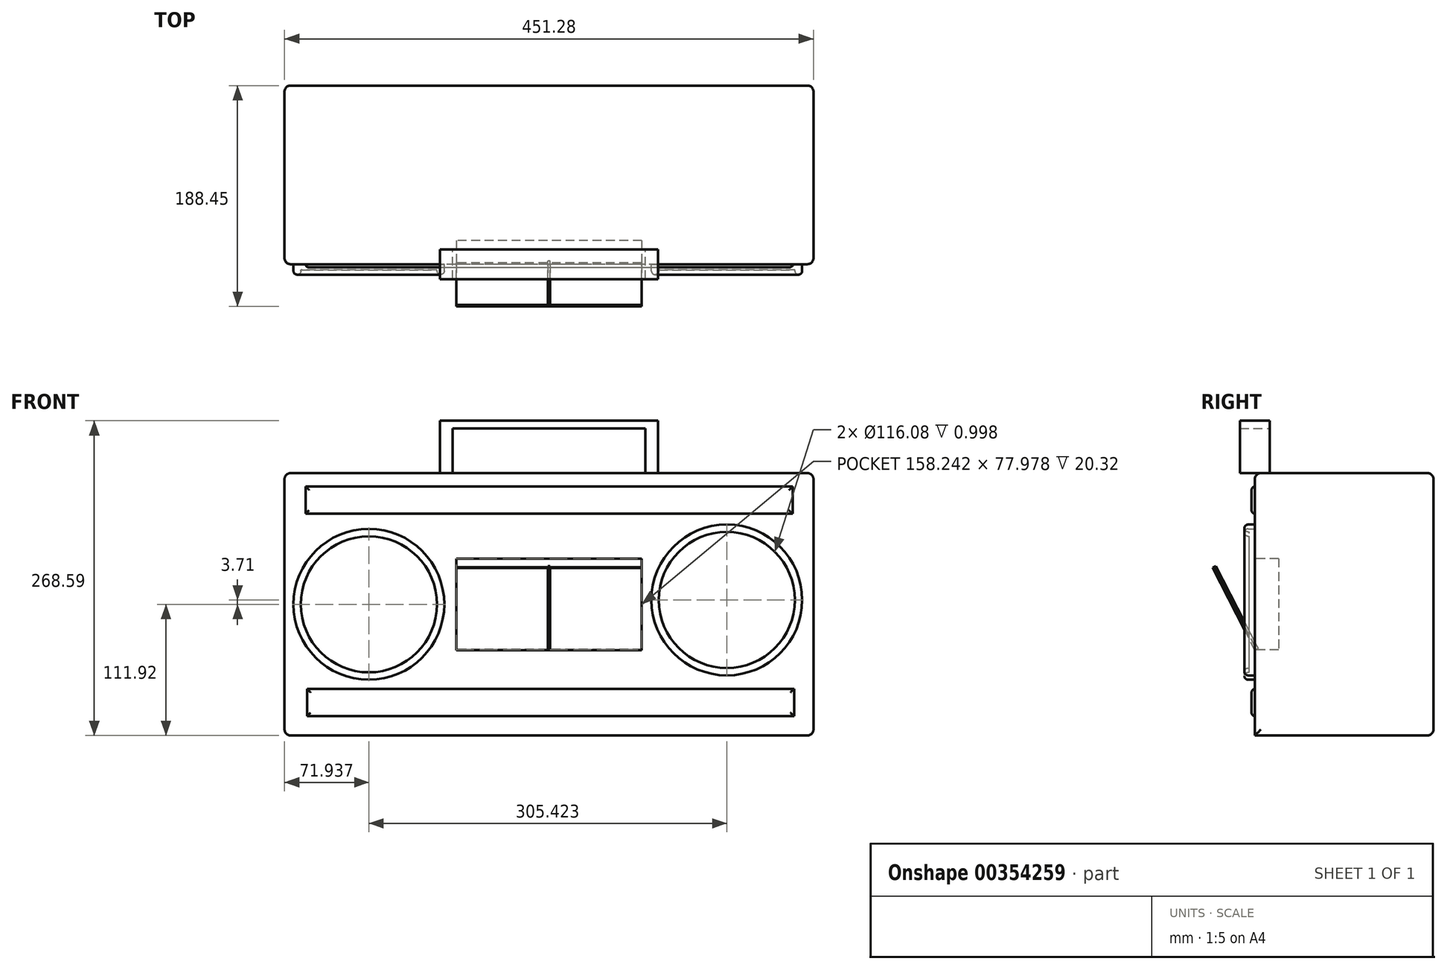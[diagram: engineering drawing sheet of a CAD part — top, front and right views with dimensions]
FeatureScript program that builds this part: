
annotation { "Feature Type Name" : "Feature", "Feature Type Description" : "" }
export const myFeature = defineFeature(function(context is Context, id is Id, definition is map)
    precondition{}
    {
        {
            var Q0;
            Q0=qCreatedBy(makeId("Front.planeOp"),FACE);
            var sketch = newSketch(context, id + "F0", { "sketchPlane" : qUnion([Q0])});
            skLineSegment(sketch, "E0.bottom", {"start": v(79.12, 38.99) * mm, "end": v(-79.12, 38.99) * mm});
            skLineSegment(sketch, "E0.top", {"start": v(79.12, -38.99) * mm, "end": v(-79.12, -38.99) * mm});
            skLineSegment(sketch, "E0.left", {"start": v(79.12, 38.99) * mm, "end": v(79.12, -38.99) * mm});
            skLineSegment(sketch, "E0.right", {"start": v(-79.12, 38.99) * mm, "end": v(-79.12, -38.99) * mm});
            skPoint(sketch, "E0.middle", {"position": v(0, 0) * mm});
            skSolve(sketch);
        }
        {
            var Q0;
            Q0=qCreatedBy(makeId("Front.planeOp"),FACE);
            var sketch = newSketch(context, id + "F1", { "sketchPlane" : qUnion([Q0])});
            skLineSegment(sketch, "E1.bottom", {"start": v(225.64, 111.92) * mm, "end": v(-225.64, 111.92) * mm});
            skLineSegment(sketch, "E1.top", {"start": v(225.64, -111.92) * mm, "end": v(-225.64, -111.92) * mm});
            skLineSegment(sketch, "E1.left", {"start": v(225.64, 111.92) * mm, "end": v(225.64, -111.92) * mm});
            skLineSegment(sketch, "E1.right", {"start": v(-225.64, 111.92) * mm, "end": v(-225.64, -111.92) * mm});
            skPoint(sketch, "E1.middle", {"position": v(0, 0) * mm});
            skSolve(sketch);
        }
        {
            var Q0;
            Q0=makeQuery(id+"F1.imprint","IMPRINT",FACE,{"disambiguationData":[TD([[makeQuery(id+"F1.imprint","IMPRINT",EDGE,{"derivedFrom":sQuery(id+"F1.wireOp",EDGE,"E1.bottom")}),1.0]])]});
            extrude(context, id + "F2", {"entities" : qUnion([Q0]), "oppositeDirection" : true, "depth" : 152.4 * mm});
        }
        {
            var Q0;
            Q0=makeQuery(id+"F0.imprint","IMPRINT",FACE,{"disambiguationData":[TD([[makeQuery(id+"F0.imprint","IMPRINT",EDGE,{"derivedFrom":sQuery(id+"F0.wireOp",EDGE,"E0.bottom")}),1.0]])]});
            extrude(context, id + "F3", {"entities" : qUnion([Q0]), "operationType" : NewBodyOperationType.REMOVE, "oppositeDirection" : true, "depth" : 20.32 * mm});
        }
        {
            var Q0;
            Q0=qCreatedBy(makeId("Front.planeOp"),FACE);
            var sketch = newSketch(context, id + "F4", { "sketchPlane" : qUnion([Q0])});
            skCircle(sketch, "E2", {"center": v(-153.7, 0) * mm, "radius": 64.33 * mm});
            skCircle(sketch, "E3", {"center": v(151.72, 3.7) * mm, "radius": 64.33 * mm});
            skCircle(sketch, "E4", {"center": v(-153.7, 0) * mm, "radius": 58.04 * mm});
            skCircle(sketch, "E5", {"center": v(151.72, 3.7) * mm, "radius": 58.04 * mm});
            skSolve(sketch);
        }
        {
            var Q0;
            Q0=makeQuery(id+"F4.imprint","IMPRINT",FACE,{"disambiguationData":[TD([[makeQuery(id+"F4.imprint","IMPRINT",EDGE,{"derivedFrom":sQuery(id+"F4.wireOp",EDGE,"E2")}),1.0]])]});
            var Q1;
            Q1=makeQuery(id+"F4.imprint","IMPRINT",FACE,{"disambiguationData":[TD([[makeQuery(id+"F4.imprint","IMPRINT",EDGE,{"derivedFrom":sQuery(id+"F4.wireOp",EDGE,"E3")}),1.0]])]});
            extrude(context, id + "F5", {"entities" : qUnion([Q0, Q1]), "operationType" : NewBodyOperationType.ADD, "depth" : 8.9 * mm});
        }
        {
            var Q0;
            Q0=makeQuery(id+"F4.imprint","IMPRINT",FACE,{"disambiguationData":[TD([[makeQuery(id+"F4.imprint","IMPRINT",EDGE,{"derivedFrom":sQuery(id+"F4.wireOp",EDGE,"E5")}),1.0]])]});
            var Q1;
            Q1=makeQuery(id+"F4.imprint","IMPRINT",FACE,{"disambiguationData":[TD([[makeQuery(id+"F4.imprint","IMPRINT",EDGE,{"derivedFrom":sQuery(id+"F4.wireOp",EDGE,"E4")}),1.0]])]});
            extrude(context, id + "F6", {"entities" : qUnion([Q0, Q1]), "operationType" : NewBodyOperationType.ADD, "depth" : 4.83 * mm});
        }
        {
            var Q0;
            Q0=qCreatedBy(makeId("Front.planeOp"),FACE);
            var sketch = newSketch(context, id + "F7", { "sketchPlane" : qUnion([Q0])});
            skLineSegment(sketch, "E6.bottom", {"start": v(207.8, 100.54) * mm, "end": v(-207.8, 100.54) * mm});
            skLineSegment(sketch, "E6.top", {"start": v(207.8, 77.23) * mm, "end": v(-207.8, 77.23) * mm});
            skLineSegment(sketch, "E6.left", {"start": v(207.8, 100.54) * mm, "end": v(207.8, 77.23) * mm});
            skLineSegment(sketch, "E6.right", {"start": v(-207.8, 100.54) * mm, "end": v(-207.8, 77.23) * mm});
            skPoint(sketch, "E6.middle", {"position": v(0, 88.89) * mm});
            skLineSegment(sketch, "E7.bottom", {"start": v(209.06, -72.15) * mm, "end": v(-206.54, -72.15) * mm});
            skLineSegment(sketch, "E7.top", {"start": v(209.06, -95.47) * mm, "end": v(-206.54, -95.47) * mm});
            skLineSegment(sketch, "E7.left", {"start": v(209.06, -72.15) * mm, "end": v(209.06, -95.47) * mm});
            skLineSegment(sketch, "E7.right", {"start": v(-206.54, -72.15) * mm, "end": v(-206.54, -95.47) * mm});
            skPoint(sketch, "E7.middle", {"position": v(1.26, -83.8) * mm});
            skSolve(sketch);
        }
        {
            var Q0;
            Q0=makeQuery(id+"F7.imprint","IMPRINT",FACE,{"disambiguationData":[TD([[makeQuery(id+"F7.imprint","IMPRINT",EDGE,{"derivedFrom":sQuery(id+"F7.wireOp",EDGE,"E6.bottom")}),1.0]])]});
            var Q1;
            Q1=makeQuery(id+"F7.imprint","IMPRINT",FACE,{"disambiguationData":[TD([[makeQuery(id+"F7.imprint","IMPRINT",EDGE,{"derivedFrom":sQuery(id+"F7.wireOp",EDGE,"E7.bottom")}),1.0]])]});
            extrude(context, id + "F8", {"entities" : qUnion([Q0, Q1]), "operationType" : NewBodyOperationType.ADD, "depth" : 2.8 * mm});
        }
        {
            var Q0;
            Q0=qCreatedBy(makeId("Right.planeOp"),FACE);
            var sketch = newSketch(context, id + "F9", { "sketchPlane" : qUnion([Q0])});
            skLineSegment(sketch, "E8", {"start": v(0, -39.04) * mm, "end": v(-36.05, 31.26) * mm});
            skLineSegment(sketch, "E9", {"start": v(-36.05, 31.26) * mm, "end": v(-33.34, 32.65) * mm});
            skLineSegment(sketch, "E10", {"start": v(0, -39.04) * mm, "end": v(2.72, -37.65) * mm});
            skLineSegment(sketch, "E11", {"start": v(-33.34, 32.65) * mm, "end": v(2.72, -37.65) * mm});
            skSolve(sketch);
        }
        {
            var Q0;
            Q0=makeQuery(id+"F9.imprint","IMPRINT",FACE,{"disambiguationData":[TD([[makeQuery(id+"F9.imprint","IMPRINT",EDGE,{"derivedFrom":sQuery(id+"F9.wireOp",EDGE,"E8")}),-1.0]])]});
            extrude(context, id + "F10", {"entities" : qUnion([Q0]), "endBound" : BoundingType.SYMMETRIC, "depth" : 1.78 * mm});
        }
        {
            var Q0;
            Q0=qCreatedBy(makeId("Right.planeOp"),FACE);
            var sketch = newSketch(context, id + "F11", { "sketchPlane" : qUnion([Q0])});
            skLineSegment(sketch, "E12", {"start": v(0, -39.04) * mm, "end": v(-35.9, 31.02) * mm});
            skLineSegment(sketch, "E13", {"start": v(-35.9, 31.02) * mm, "end": v(-34.7, 31.64) * mm});
            skLineSegment(sketch, "E14", {"start": v(-34.7, 31.64) * mm, "end": v(1.23, -38.47) * mm});
            skLineSegment(sketch, "E15", {"start": v(1.23, -38.47) * mm, "end": v(0, -39.04) * mm});
            skSolve(sketch);
        }
        {
            var Q0;
            Q0 = qSketchRegion(id + "F11", true);
            extrude(context, id + "F12", {"entities" : qUnion([Q0]), "endBound" : BoundingType.SYMMETRIC, "depth" : 158 * mm});
        }
        {
            var Q0;
            Q0=qCreatedBy(makeId("Front.planeOp"),FACE);
            var sketch = newSketch(context, id + "F13", { "sketchPlane" : qUnion([Q0])});
            skLineSegment(sketch, "E16", {"start": v(-82.27, 112.02) * mm, "end": v(-82.27, 150.12) * mm});
            skLineSegment(sketch, "E17", {"start": v(-82.27, 150.12) * mm, "end": v(0, 150.12) * mm});
            skLineSegment(sketch, "E18.MirrorCS", {"start": v(82.27, 150.12) * mm, "end": v(0, 150.12) * mm});
            skLineSegment(sketch, "E19.MirrorCS", {"start": v(82.27, 112.02) * mm, "end": v(82.27, 150.12) * mm});
            skLineSegment(sketch, "E20", {"start": v(-93.02, 112.02) * mm, "end": v(-93.02, 150.12) * mm});
            skLineSegment(sketch, "E21", {"start": v(-93.02, 150.12) * mm, "end": v(-93.02, 156.67) * mm});
            skLineSegment(sketch, "E22", {"start": v(-93.02, 156.67) * mm, "end": v(0, 156.67) * mm});
            skLineSegment(sketch, "E23.MirrorCS", {"start": v(93.02, 156.67) * mm, "end": v(0, 156.67) * mm});
            skLineSegment(sketch, "E24.MirrorCS", {"start": v(93.02, 150.12) * mm, "end": v(93.02, 156.67) * mm});
            skLineSegment(sketch, "E25.MirrorCS", {"start": v(93.02, 112.02) * mm, "end": v(93.02, 150.12) * mm});
            skLineSegment(sketch, "E26", {"start": v(-93.02, 112.02) * mm, "end": v(-82.27, 112.02) * mm});
            skLineSegment(sketch, "E27", {"start": v(82.27, 112.02) * mm, "end": v(93.02, 112.02) * mm});
            skSolve(sketch);
        }
        {
            var Q0;
            Q0=makeQuery(id+"F13.imprint","IMPRINT",FACE,{"disambiguationData":[TD([[makeQuery(id+"F13.imprint","IMPRINT",EDGE,{"derivedFrom":sQuery(id+"F13.wireOp",EDGE,"E16")}),1.0]])]});
            extrude(context, id + "F14", {"entities" : qUnion([Q0]), "endBound" : BoundingType.SYMMETRIC, "depth" : 25.4 * mm});
        }
        {
            var Q0;
            Q0=makeQuery(id+"F5.opExtrude","CAP_EDGE",EDGE,{"disambiguationData":[OSD([sQuery(id+"F4.wireOp",EDGE,"E4")])],"isStart":false});
            var Q1;
            Q1=makeQuery(id+"F5.opExtrude","CAP_EDGE",EDGE,{"disambiguationData":[OSD([sQuery(id+"F4.wireOp",EDGE,"E2")])],"isStart":false});
            var Q2;
            Q2=makeQuery(id+"F5.opExtrude","CAP_EDGE",EDGE,{"disambiguationData":[OSD([sQuery(id+"F4.wireOp",EDGE,"E3")])],"isStart":false});
            var Q3;
            Q3=makeQuery(id+"F5.opExtrude","CAP_EDGE",EDGE,{"disambiguationData":[OSD([sQuery(id+"F4.wireOp",EDGE,"E5")])],"isStart":false});
            fillet(context, id + "F15", {"entities" : qUnion([Q0, Q1, Q2, Q3]), "radius" : 3.07 * mm, "tangentPropagation" : true, "allowEdgeOverflow" : false});
        }
        {
            var Q0;
            Q0=makeQuery(id+"F8.opExtrude","CAP_EDGE",EDGE,{"disambiguationData":[OSD([sQuery(id+"F7.wireOp",EDGE,"E6.bottom")])],"isStart":false});
            var Q1;
            Q1=makeQuery(id+"F8.opExtrude","CAP_EDGE",EDGE,{"disambiguationData":[OSD([sQuery(id+"F7.wireOp",EDGE,"E6.top")])],"isStart":false});
            var Q2;
            Q2=makeQuery(id+"F8.opExtrude","CAP_EDGE",EDGE,{"disambiguationData":[OSD([sQuery(id+"F7.wireOp",EDGE,"E6.right")])],"isStart":false});
            var Q3;
            Q3=makeQuery(id+"F8.opExtrude","CAP_EDGE",EDGE,{"disambiguationData":[OSD([sQuery(id+"F7.wireOp",EDGE,"E6.left")])],"isStart":false});
            var Q4;
            Q4=makeQuery(id+"F8.opExtrude","CAP_EDGE",EDGE,{"disambiguationData":[OSD([sQuery(id+"F7.wireOp",EDGE,"E7.bottom")])],"isStart":false});
            var Q5;
            Q5=makeQuery(id+"F8.opExtrude","CAP_EDGE",EDGE,{"disambiguationData":[OSD([sQuery(id+"F7.wireOp",EDGE,"E7.left")])],"isStart":false});
            var Q6;
            Q6=makeQuery(id+"F8.opExtrude","CAP_EDGE",EDGE,{"disambiguationData":[OSD([sQuery(id+"F7.wireOp",EDGE,"E7.top")])],"isStart":false});
            var Q7;
            Q7=makeQuery(id+"F8.opExtrude","CAP_EDGE",EDGE,{"disambiguationData":[OSD([sQuery(id+"F7.wireOp",EDGE,"E7.right")])],"isStart":false});
            fillet(context, id + "F16", {"entities" : qUnion([Q0, Q1, Q2, Q3, Q4, Q5, Q6, Q7]), "radius" : 3.07 * mm, "tangentPropagation" : true, "allowEdgeOverflow" : false});
        }
        {
            var Q0;
            Q0=makeQuery(id+"F2.opExtrude","CAP_EDGE",EDGE,{"disambiguationData":[OSD([sQuery(id+"F1.wireOp",EDGE,"E1.right")])],"isStart":true});
            var Q1;
            Q1=makeQuery(id+"F2.opExtrude","CAP_EDGE",EDGE,{"disambiguationData":[OSD([sQuery(id+"F1.wireOp",EDGE,"E1.right")])],"isStart":false});
            var Q2;
            Q2=makeQuery(id+"F2.opExtrude","CAP_EDGE",EDGE,{"disambiguationData":[OSD([sQuery(id+"F1.wireOp",EDGE,"E1.left")])],"isStart":true});
            var Q3;
            Q3=makeQuery(id+"F2.opExtrude","CAP_EDGE",EDGE,{"disambiguationData":[OSD([sQuery(id+"F1.wireOp",EDGE,"E1.left")])],"isStart":false});
            var Q4;
            Q4=makeQuery(id+"F2.opExtrude","SWEPT_EDGE",EDGE,{"disambiguationData":[OSD([sQuery(id+"F1.wireOp",EDGE,"E1.top"),sQuery(id+"F1.wireOp",EDGE,"E1.left")])]});
            var Q5;
            Q5=makeQuery(id+"F2.opExtrude","SWEPT_EDGE",EDGE,{"disambiguationData":[OSD([sQuery(id+"F1.wireOp",EDGE,"E1.bottom"),sQuery(id+"F1.wireOp",EDGE,"E1.left")])]});
            var Q6;
            Q6=makeQuery(id+"F2.opExtrude","CAP_EDGE",EDGE,{"disambiguationData":[OSD([sQuery(id+"F1.wireOp",EDGE,"E1.bottom")])],"isStart":true});
            var Q7;
            Q7=makeQuery(id+"F2.opExtrude","CAP_EDGE",EDGE,{"disambiguationData":[OSD([sQuery(id+"F1.wireOp",EDGE,"E1.bottom")])],"isStart":false});
            var Q8;
            Q8=makeQuery(id+"F2.opExtrude","CAP_EDGE",EDGE,{"disambiguationData":[OSD([sQuery(id+"F1.wireOp",EDGE,"E1.top")])],"isStart":false});
            var Q9;
            Q9=makeQuery(id+"F2.opExtrude","SWEPT_EDGE",EDGE,{"disambiguationData":[OSD([sQuery(id+"F1.wireOp",EDGE,"E1.top"),sQuery(id+"F1.wireOp",EDGE,"E1.right")])]});
            var Q10;
            Q10=makeQuery(id+"F2.opExtrude","SWEPT_EDGE",EDGE,{"disambiguationData":[OSD([sQuery(id+"F1.wireOp",EDGE,"E1.bottom"),sQuery(id+"F1.wireOp",EDGE,"E1.right")])]});
            fillet(context, id + "F17", {"entities" : qUnion([Q0, Q1, Q2, Q3, Q4, Q5, Q6, Q7, Q8, Q9, Q10]), "radius" : 5.08 * mm, "tangentPropagation" : true, "allowEdgeOverflow" : false});
        }
    });
